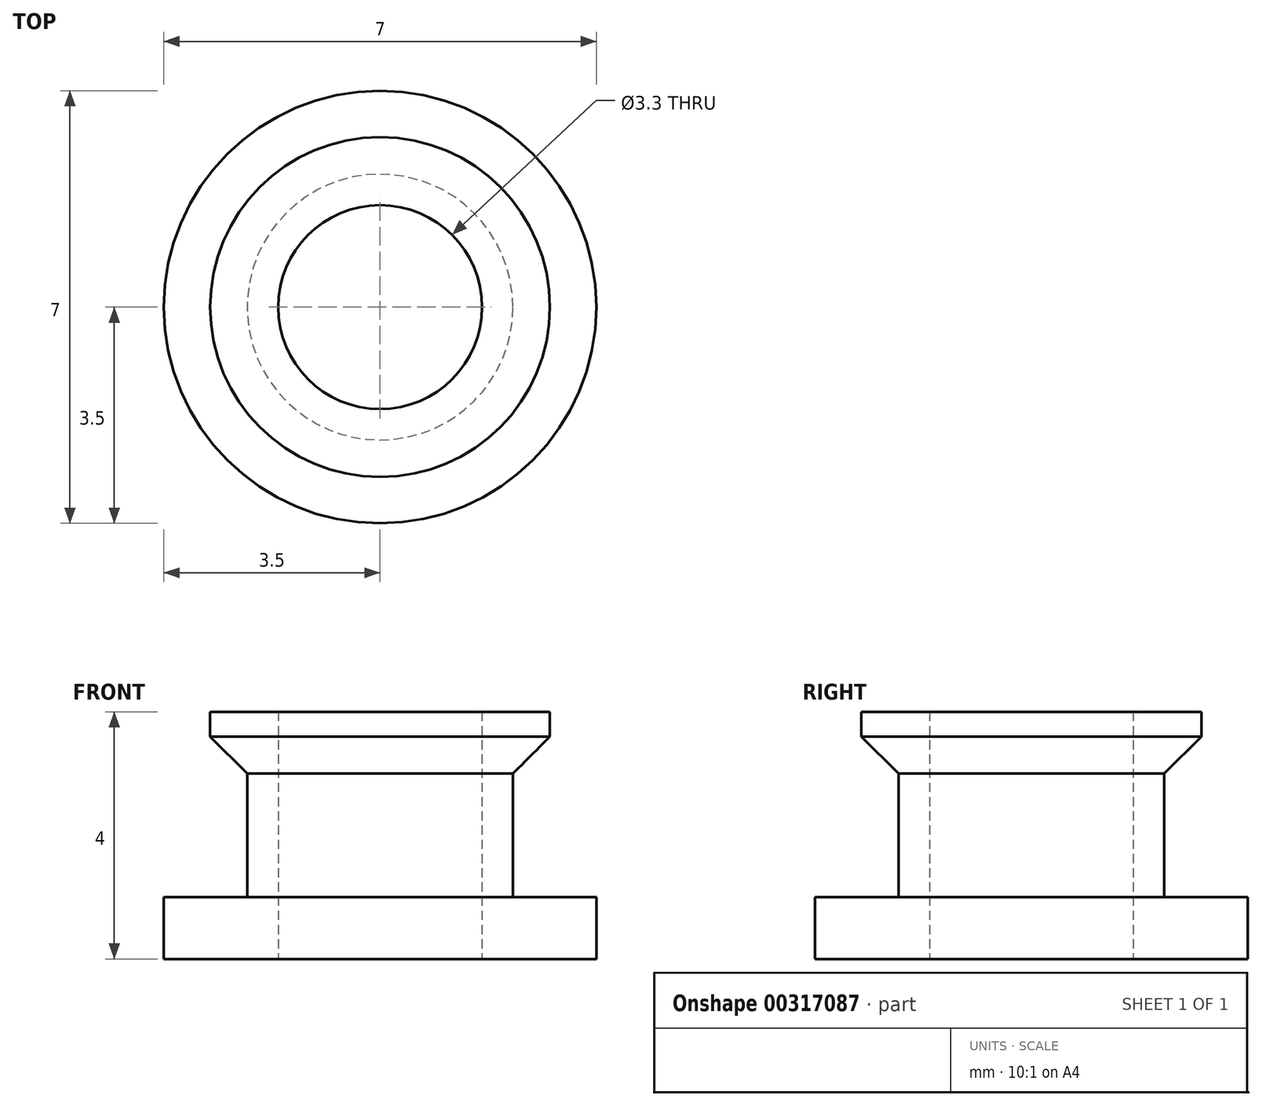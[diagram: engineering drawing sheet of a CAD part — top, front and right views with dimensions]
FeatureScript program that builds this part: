
annotation { "Feature Type Name" : "Feature", "Feature Type Description" : "" }
export const myFeature = defineFeature(function(context is Context, id is Id, definition is map)
    precondition{}
    {
        {
            var Q0;
            Q0=qCreatedBy(makeId("Top.planeOp"),FACE);
            var sketch = newSketch(context, id + "F0", { "sketchPlane" : qUnion([Q0])});
            skCircle(sketch, "E0", {"center": v(0, 0) * mm, "radius": 1.65 * mm});
            skCircle(sketch, "E1", {"center": v(0, 0) * mm, "radius": 2.15 * mm});
            skCircle(sketch, "E2", {"center": v(0, 0) * mm, "radius": 3.5 * mm});
            skSolve(sketch);
        }
        {
            var Q0;
            Q0=makeQuery(id+"F0.imprint","IMPRINT",FACE,{"disambiguationData":[TD([[makeQuery(id+"F0.imprint","IMPRINT",EDGE,{"derivedFrom":sQuery(id+"F0.wireOp",EDGE,"E0")}),-1.0]])]});
            var Q1;
            Q1=makeQuery(id+"F0.imprint","IMPRINT",FACE,{"disambiguationData":[TD([[makeQuery(id+"F0.imprint","IMPRINT",EDGE,{"derivedFrom":sQuery(id+"F0.wireOp",EDGE,"E1")}),-1.0]])]});
            extrude(context, id + "F1", {"entities" : qUnion([Q0, Q1]), "depth" : 1 * mm});
        }
        {
            var Q0;
            Q0=makeQuery(id+"F1.opExtrude","CAP_FACE",FACE,{"disambiguationData":[OSD([sQuery(id+"F0.wireOp",EDGE,"E0"),sQuery(id+"F0.wireOp",EDGE,"E2")])],"isStart":false});
            var sketch = newSketch(context, id + "F2", { "sketchPlane" : qUnion([Q0])});
            skCircle(sketch, "E3", {"center": v(0, 0) * mm, "radius": 2.15 * mm});
            skSolve(sketch);
        }
        {
            var Q0;
            Q0=makeQuery(id+"F2.imprint","IMPRINT",FACE,{"disambiguationData":[TD([[makeQuery(id+"F2.imprint","IMPRINT",EDGE,{"derivedFrom":sQuery(id+"F2.wireOp",EDGE,"E3")}),1.0]])]});
            extrude(context, id + "F3", {"entities" : qUnion([Q0]), "operationType" : NewBodyOperationType.ADD, "depth" : 2 * mm});
        }
        {
            var Q0;
            Q0=makeQuery(id+"F3.opExtrude","CAP_FACE",FACE,{"disambiguationData":[OSD([sQuery(id+"F0.wireOp",EDGE,"E0"),sQuery(id+"F2.wireOp",EDGE,"E3")])],"isStart":false});
            var sketch = newSketch(context, id + "F4", { "sketchPlane" : qUnion([Q0])});
            skCircle(sketch, "E4", {"center": v(0, 0) * mm, "radius": 2.75 * mm});
            skSolve(sketch);
        }
        {
            var Q0;
            Q0=makeQuery(id+"F4.imprint","IMPRINT",FACE,{"disambiguationData":[TD([[makeQuery(id+"F4.imprint","IMPRINT",EDGE,{"derivedFrom":makeQuery(id+"F3.opExtrude","CAP_EDGE",EDGE,{"disambiguationData":[OSD([sQuery(id+"F2.wireOp",EDGE,"E3")])],"isStart":false})}),1.0]])]});
            var Q1;
            Q1=makeQuery(id+"F4.imprint","IMPRINT",FACE,{"disambiguationData":[TD([[makeQuery(id+"F4.imprint","IMPRINT",EDGE,{"derivedFrom":sQuery(id+"F4.wireOp",EDGE,"E4")}),1.0]])]});
            extrude(context, id + "F5", {"entities" : qUnion([Q0, Q1]), "operationType" : NewBodyOperationType.ADD, "depth" : 1 * mm});
        }
        {
            var Q0;
            Q0=makeQuery(id+"F5.opExtrude","CAP_EDGE",EDGE,{"disambiguationData":[OSD([sQuery(id+"F4.wireOp",EDGE,"E4")])],"isStart":true});
            chamfer(context, id + "F6", {"entities" : qUnion([Q0]), "width" : .6 * mm, "tangentPropagation" : true});
        }
    });
